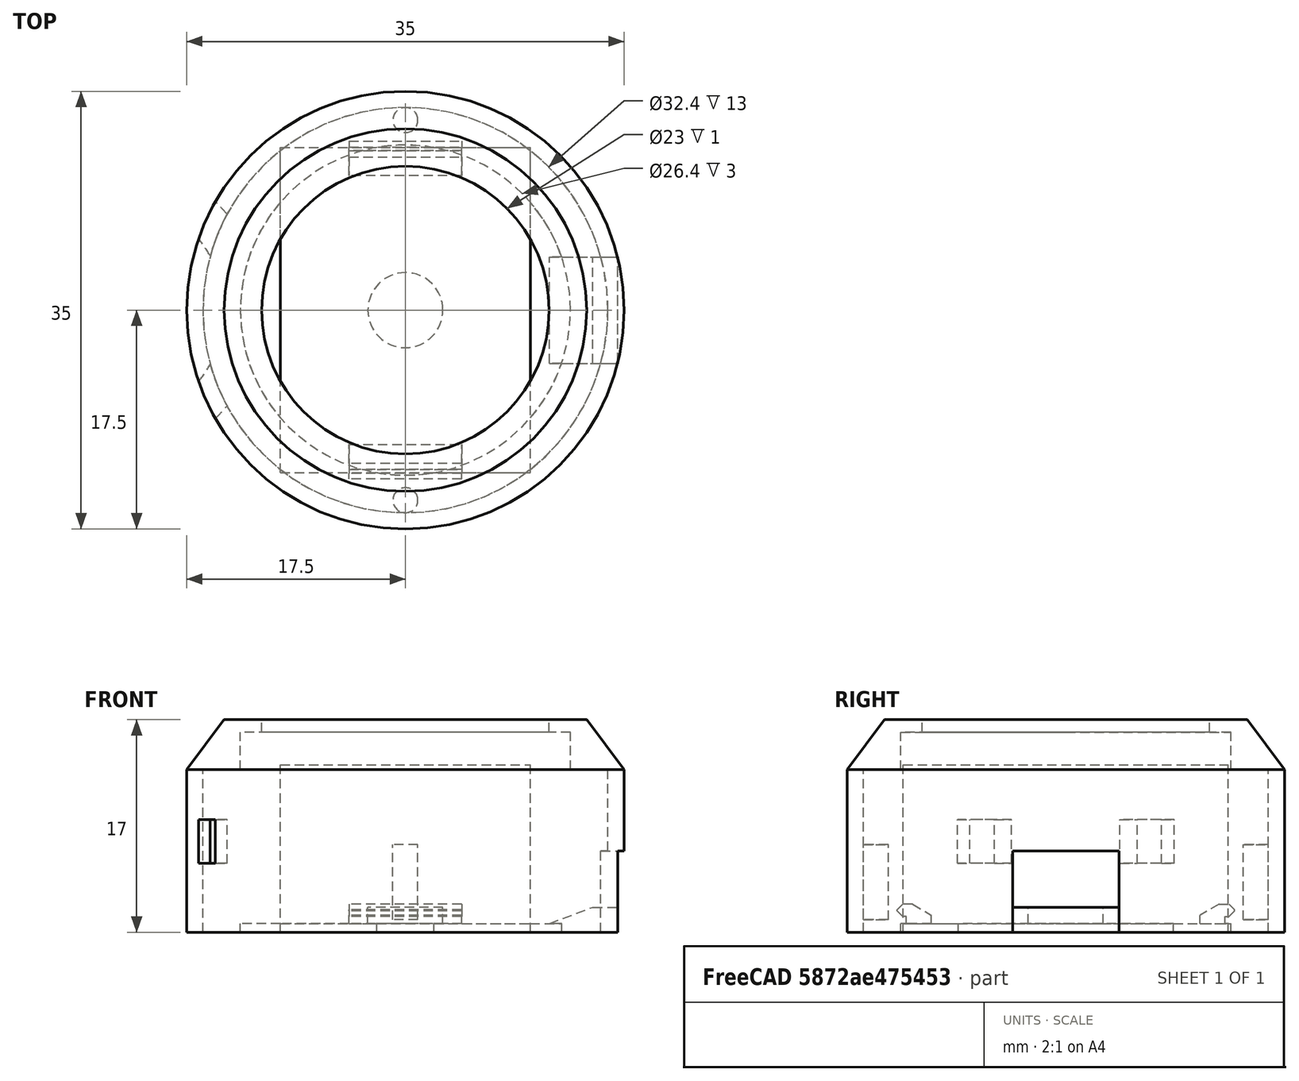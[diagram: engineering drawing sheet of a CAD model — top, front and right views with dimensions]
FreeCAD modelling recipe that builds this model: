
FCSTD DOCUMENT  (FreeCAD 0.15R4630 (Git))
Label: Pendant Shell
License: All rights reserved
LicenseURL: http://en.wikipedia.org/wiki/All_rights_reserved
objects: Part::Cylinder×10, Part::Box×8, Part::Chamfer×5, Part::MultiFuse×3, Part::Cut×2
note: 28 computed .brp shape members not serialized (recipe doc carries the construction recipe); baked Part::Feature solids carry a one-line shape summary decoded from their .brp

FEATURE [Part::Cylinder] Cylinder002  label="DiffuserHole"
  Angle = 360
  Height = 30
  Radius = 11.5
FEATURE [Part::Cylinder] Cylinder  label="PCB Hole"
  Angle = 360
  Height = 16
  Placement = pos=(0,0,-1) rot=(0,0,1;0rad)
  Radius = 13.2
FEATURE [Part::Cylinder] Cylinder006  label="MainBody"
  Angle = 360
  Height = 17
  Placement = pos=(0,0,-1) rot=(0,0,1;0rad)
  Radius = 17.5
FEATURE [Part::Box] Box  label="BatteryHole"
  Height = 13.4
  Length = 20
  Placement = pos=(-10,-13,-1) rot=(0,0,1;0rad)
  Width = 26
FEATURE [Part::Box] Box001  label="USB"
  Height = 7
  Length = 16
  Placement = pos=(7,-4.25,-1.5) rot=(0,0,1;0rad)
  Width = 8.5
FEATURE [Part::Cylinder] Cylinder007  label="R Screw"
  Angle = 360
  Height = 6
  Placement = pos=(0,-15.2,0) rot=(0,0,1;0rad)
  Radius = 1
FEATURE [Part::Cylinder] Cylinder008  label="L Screw"
  Angle = 360
  Height = 6
  Placement = pos=(0,15.2,0) rot=(0,0,1;0rad)
  Radius = 1
FEATURE [Part::Chamfer] Chamfer  label="MainBody Chamfered"
  Base = -> Cylinder006
  Edges = 1 edges: [Edge1 r1=4 r2=3]
FEATURE [Part::Cylinder] Cylinder016  label="Button Presser"
  Angle = 360
  Height = 1.5
  Placement = pos=(0,0,-0.5) rot=(0,0,1;0rad)
  Radius = 3
FEATURE [Part::Cylinder] Cylinder017  label="Cylinder"
  Angle = 360
  Height = 3.5
  Placement = pos=(-23.5,0,4.5) rot=(0,0,1;0rad)
  Radius = 12
FEATURE [Part::Cylinder] Cylinder018  label="Cylinder001"
  Angle = 360
  Height = 3.5
  Placement = pos=(-23.5,0,4.5) rot=(0,0,1;0rad)
  Radius = 9
FEATURE [Part::Cut] Cut002  label="Chain Channel"
  Base = -> Cylinder017
  Tool = -> Cylinder018
FEATURE [Part::Box] Box002  label="BatteryHole001"
  Height = 0.7
  Length = 20
  Placement = pos=(-10,-13,-1) rot=(0,0,1;0rad)
  Width = 26
FEATURE [Part::Cylinder] Cylinder019  label="PCB Hole001"
  Angle = 360
  Height = 0.7
  Placement = pos=(0,0,-1) rot=(0,0,1;0rad)
  Radius = 13.2
FEATURE [Part::Box] Box003  label="USB Cover Base"
  Height = 2
  Length = 6
  Placement = pos=(11,-4.25,-1) rot=(0,0,1;0rad)
  Width = 8.5
FEATURE [Part::Box] Box004  label="Tab"
  Height = 1
  Length = 9
  Placement = pos=(-4.5,10.75,0.25) rot=(0,0,1;0rad)
  Width = 2.75
FEATURE [Part::Box] Box006  label="Tab 2 Female"
  Height = 1.5
  Length = 10
  Placement = pos=(-5,-14,0) rot=(0,0,1;0rad)
  Width = 2
FEATURE [Part::Box] Box007  label="Tab 1 Female"
  Height = 1.5
  Length = 10
  Placement = pos=(-5,12,0) rot=(0,0,1;0rad)
  Width = 2
FEATURE [Part::Chamfer] Chamfer004  label="USB Cover"
  Base = -> Box003
  Edges = 1 edges: [Edge2 r1=1.5 r2=4]
FEATURE [Part::Box] Box008  label="Tab Base"
  Height = 1
  Length = 9
  Placement = pos=(-4.5,10.75,-0.75) rot=(0,0,1;0rad)
  Width = 2
FEATURE [Part::MultiFuse] Fusion002
  Shapes = -> [Box004,Box008]
FEATURE [Part::Chamfer] Chamfer005
  Base = -> Fusion002
  Edges = 1 edges: [Edge4 r1=1.5 r2=0.9]
FEATURE [Part::Chamfer] Chamfer006  label="Tab 2"
  Base = -> Chamfer005
  Edges = 2 edges r=0.45: [Edge3,Edge12]
  Placement = pos=(0,0,0) rot=(0,0,1;3.14159rad)
FEATURE [Part::Chamfer] Chamfer007  label="Tab 1"
  Base = -> Chamfer005
  Edges = 2 edges r=0.45: [Edge3,Edge12]
FEATURE [Part::MultiFuse] Fusion001  label="Back"
  Shapes = -> [Cylinder019,Box002,Cylinder016,Chamfer004,Chamfer006,Chamfer007]
FEATURE [Part::Cylinder] Cylinder020  label="Hollow Out"
  Angle = 360
  Height = 13
  Placement = pos=(0,0,-1) rot=(0,0,1;0rad)
  Radius = 16.2
FEATURE [Part::MultiFuse] Fusion  label="Guts"
  Shapes = -> [Cylinder,Cylinder002,Box001,Cut002,Box006,Box007,Cylinder020]
FEATURE [Part::Cut] Cut  label="Front"
  Base = -> Chamfer
  Tool = -> Fusion
